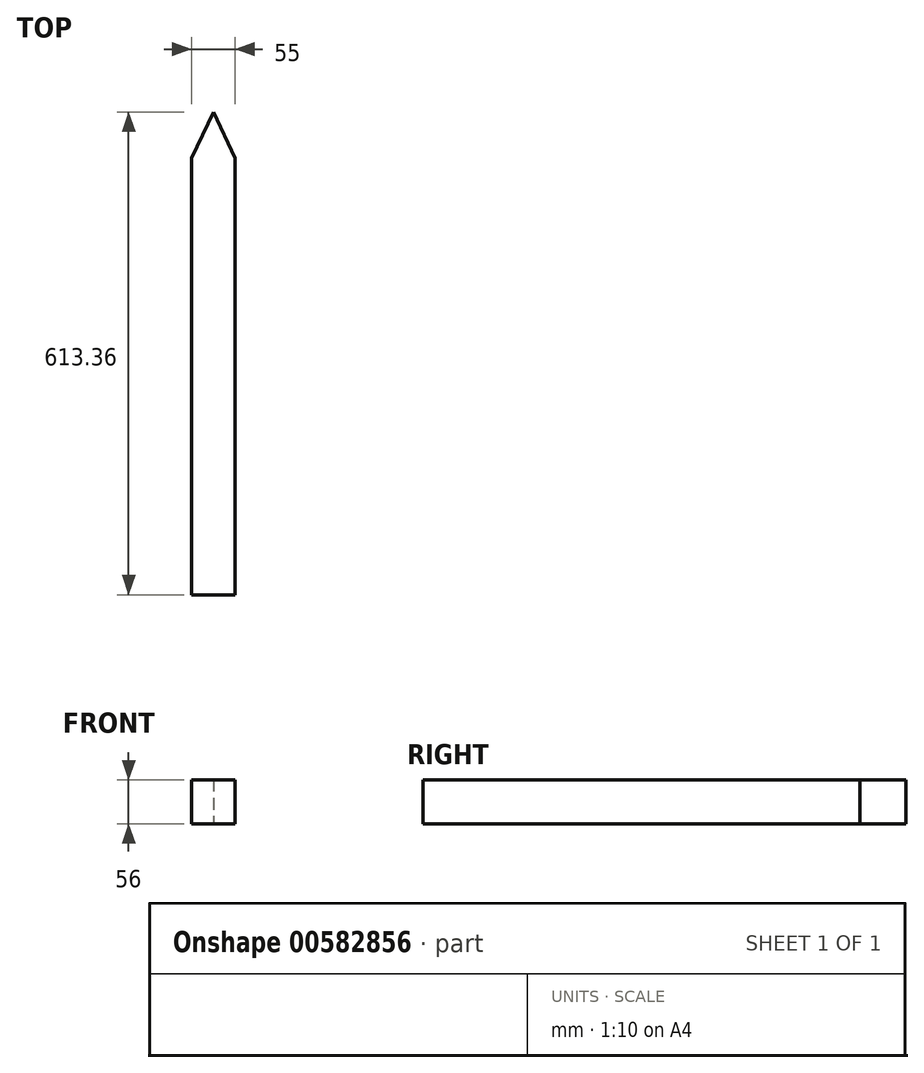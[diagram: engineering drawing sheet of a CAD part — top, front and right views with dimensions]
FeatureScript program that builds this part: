
annotation { "Feature Type Name" : "Feature", "Feature Type Description" : "" }
export const myFeature = defineFeature(function(context is Context, id is Id, definition is map)
    precondition{}
    {
        {
            var Q0;
            Q0=qCreatedBy(makeId("Top.planeOp"),FACE);
            var sketch = newSketch(context, id + "F0", { "sketchPlane" : qUnion([Q0])});
            skLineSegment(sketch, "E0.bottom", {"start": v(0, 0) * mm, "end": v(-55, 0) * mm});
            skLineSegment(sketch, "E0.top", {"start": v(0, 555) * mm, "end": v(-55, 555) * mm});
            skLineSegment(sketch, "E0.left", {"start": v(0, 0) * mm, "end": v(0, 555) * mm});
            skLineSegment(sketch, "E0.right", {"start": v(-55, 0) * mm, "end": v(-55, 555) * mm});
            skLineSegment(sketch, "E1", {"start": v(-55, 555) * mm, "end": v(-27.5, 613.36) * mm});
            skPoint(sketch, "E1.endSnap0", {"position": v(-27.5, 555) * mm});
            skLineSegment(sketch, "E2", {"start": v(-27.5, 613.36) * mm, "end": v(0, 555) * mm});
            skSolve(sketch);
        }
        {
            var Q0;
            Q0=makeQuery(id+"F0.imprint","IMPRINT",FACE,{"disambiguationData":[TD([[makeQuery(id+"F0.imprint","IMPRINT",EDGE,{"derivedFrom":sQuery(id+"F0.wireOp",EDGE,"E0.bottom")}),-1.0]])]});
            var Q1;
            Q1=makeQuery(id+"F0.imprint","IMPRINT",FACE,{"disambiguationData":[TD([[makeQuery(id+"F0.imprint","IMPRINT",EDGE,{"derivedFrom":sQuery(id+"F0.wireOp",EDGE,"E0.top")}),-1.0]])]});
            extrude(context, id + "F1", {"entities" : qUnion([Q0, Q1]), "depth" : 56 * mm, "offsetDistance" : 25 * mm});
        }
    });
